FCSTD DOCUMENT  (FreeCAD 0.19R24276 (Git))
Label: Master_sketch
License: All rights reserved
LicenseURL: http://en.wikipedia.org/wiki/All_rights_reserved
objects: Sketcher::SketchObject×1, PartDesign::Body×1
note: 2 computed .brp shape members not serialized (recipe doc carries the construction recipe); baked Part::Feature solids carry a one-line shape summary decoded from their .brp

FEATURE [Sketcher::SketchObject] Sketch
  FullyConstrained = false
  MapMode = 5
  Support = -> [XY_Plane]
  sketch-geometry (8):
    g0: LineSegment StartX=0 StartY=0 StartZ=0 EndX=36.9413 EndY=0 EndZ=0
    g1: LineSegment StartX=36.9413 StartY=0 StartZ=0 EndX=36.9413 EndY=4 EndZ=0
    g2: LineSegment StartX=36.9413 StartY=4 StartZ=0 EndX=0 EndY=4 EndZ=0
    g3: LineSegment StartX=0 StartY=4 StartZ=0 EndX=0 EndY=0 EndZ=0
    g4: LineSegment StartX=66.7483 StartY=0 StartZ=0 EndX=98.8186 EndY=0 EndZ=0
    g5: LineSegment StartX=98.8186 StartY=0 StartZ=0 EndX=98.8186 EndY=6 EndZ=0
    g6: LineSegment StartX=98.8186 StartY=6 StartZ=0 EndX=66.7483 EndY=6 EndZ=0
    g7: LineSegment StartX=66.7483 StartY=6 StartZ=0 EndX=66.7483 EndY=0 EndZ=0
  constraints (20):
    c: Coincident(g0,g1)
    c: Coincident(g1,g2)
    c: Coincident(g2,g3)
    c: Coincident(g3,g0)
    c: Horizontal(g0)
    c: Horizontal(g2)
    c: Vertical(g1)
    c: Vertical(g3)
    c: Coincident(g0,g-1)
    c: DistanceY(g1,g1) = 4
    c: Coincident(g4,g5)
    c: Coincident(g5,g6)
    c: Coincident(g6,g7)
    c: Coincident(g7,g4)
    c: Horizontal(g4)
    c: Horizontal(g6)
    c: Vertical(g5)
    c: Vertical(g7)
    c: PointOnObject(g4,g-1)
    c: DistanceY(g5,g5) = 6
FEATURE [PartDesign::Body] Body
  Group = -> [Sketch]
  Origin = -> Origin
